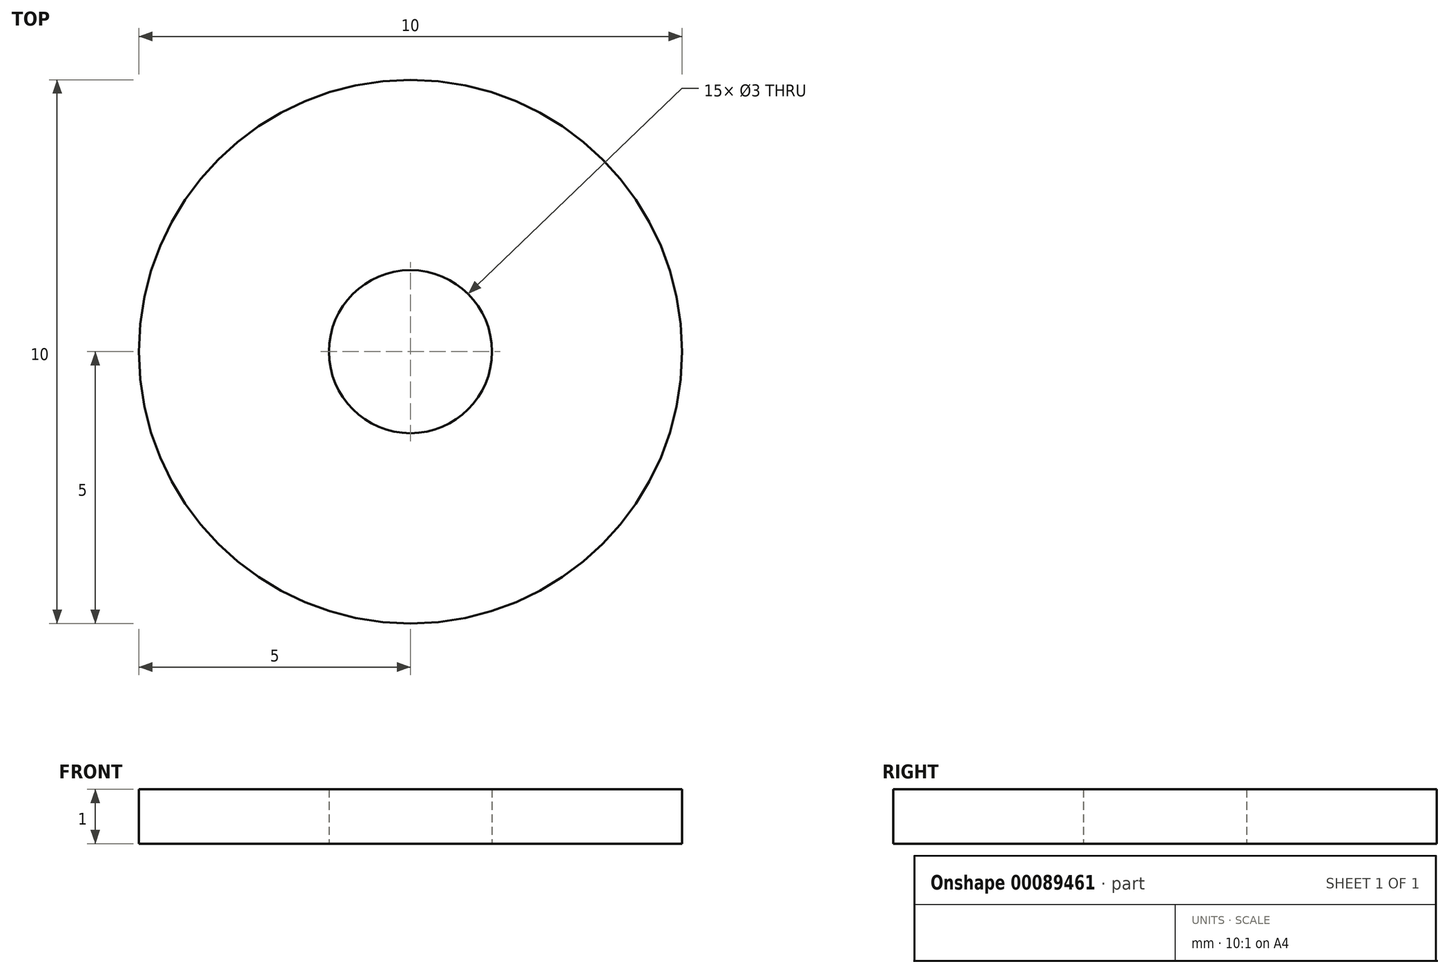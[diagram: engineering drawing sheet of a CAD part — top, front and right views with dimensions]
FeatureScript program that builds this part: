
annotation { "Feature Type Name" : "Feature", "Feature Type Description" : "" }
export const myFeature = defineFeature(function(context is Context, id is Id, definition is map)
    precondition{}
    {
        {
            var Q0;
            Q0=qCreatedBy(makeId("Top.planeOp"),FACE);
            var sketch = newSketch(context, id + "F0", { "sketchPlane" : qUnion([Q0])});
            skCircle(sketch, "E0", {"center": v(0, 0) * mm, "radius": 1.5 * mm});
            skCircle(sketch, "E1", {"center": v(0, 0) * mm, "radius": 5 * mm});
            skSolve(sketch);
        }
        {
            var Q0;
            Q0 = qSketchRegion(id + "F0", true);
            extrude(context, id + "F1", {"entities" : qUnion([Q0]), "depth" : 1 * mm});
        }
    });
